# Revit family: FP-Revit20-en-DD60DI9-DoubleDishDrawer-0-90000902B-AU-NZ-SG
name_source: partatom
category: Specialty Equipment
units: mm (PartAtom-declared; Revit-internal decimal feet)

## family parameters
Always vertical = Yes
Cut with Voids When Loaded = Yes
OmniClass Number = 23.40.40.14.31
OmniClass Title = Cleaning and Disposal Equipment
Part Type = Normal
Room Calculation Point = No
Round Connector Dimension = Use Diameter
Shared = No
Work Plane-Based = No

## types (2) — shared parameters
Cavity - Depth = 560 mm  [stored 1.83727 ft]
Cavity - Width = 600 mm  [stored 1.9685 ft]
Chassis - Height (855mm Tall or 811mm Std) = 811 mm  [stored 2.66076 ft]
Connector Description - Electrical = 230 V, 15 A, fused electrical supply
Connector Description - Sanitary = Drain Hose, No Fitting Required
Connector Description - Water = 3/4“ BSP (GB20) to suit Flat Washer
Description = Integrated Double DishDrawer
Manufacturer = Fisher & Paykel Appliances
Material - Body = Fisher & Paykel - Grey
Material - Door Front = Fisher & Paykel - Stainless Steel
Material - Door Structure = Fisher & Paykel - Aluminium
Material - Handle = Fisher & Paykel - Aluminium, Dark
Material - Toe Kick = Fisher & Paykel - Aluminium, Dark, Matt
Material - Trim = Fisher & Paykel - Black
Panel - Depth (default) = 18 mm  [stored 0.0590551 ft]
Product - Depth = 553 mm  [stored 1.8143 ft]
Product - Width = 599 mm  [stored 1.96522 ft]
URL = www.fisherpaykel.com
Visibility - Clearance Required = Yes
Visibility - Door Panel = No
Visibility - Handle = No
Visibility - Toe Kick = Yes
zero-valued in all types: Cavity - Height, Default Elevation

## type names (no varying parameters)
- DD60DI9
- DD60DHI9

note: column(s) folded — value = type name in every type: Model

note: [stored X ft] marks values corroborated as IEEE doubles in the binary element streams (Revit-internal decimal feet)

## geometry (parser evidence)
native form markers: Sweep x6
no freeform markers — native parametric forms only
